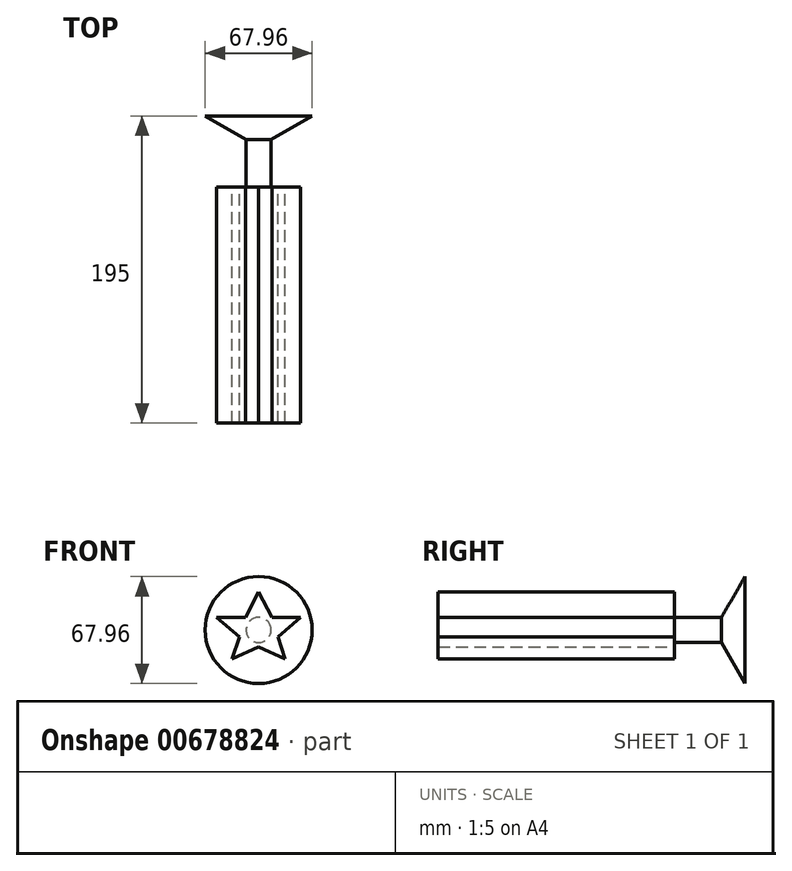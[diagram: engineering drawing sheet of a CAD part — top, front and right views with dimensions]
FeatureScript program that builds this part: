
annotation { "Feature Type Name" : "Feature", "Feature Type Description" : "" }
export const myFeature = defineFeature(function(context is Context, id is Id, definition is map)
    precondition{}
    {
        {
            var Q0;
            Q0=qCreatedBy(makeId("Front.planeOp"),FACE);
            var sketch = newSketch(context, id + "F0", { "sketchPlane" : qUnion([Q0])});
            skLineSegment(sketch, "E0", {"start": v(0, 24.1) * mm, "end": v(8.38, 8) * mm});
            skLineSegment(sketch, "E1", {"start": v(8.38, 8) * mm, "end": v(26.77, 8) * mm});
            skLineSegment(sketch, "E2", {"start": v(26.77, 8) * mm, "end": v(12.19, -4.45) * mm});
            skLineSegment(sketch, "E3", {"start": v(12.19, -4.45) * mm, "end": v(16.83, -18.28) * mm});
            skLineSegment(sketch, "E4", {"start": v(16.83, -18.28) * mm, "end": v(0, -10.61) * mm});
            skLineSegment(sketch, "E5.MirrorCS", {"start": v(0, 24.1) * mm, "end": v(-8.38, 8) * mm});
            skLineSegment(sketch, "E6.MirrorCS", {"start": v(-8.38, 8) * mm, "end": v(-26.77, 8) * mm});
            skLineSegment(sketch, "E7.MirrorCS", {"start": v(-26.77, 8) * mm, "end": v(-12.19, -4.45) * mm});
            skLineSegment(sketch, "E8.MirrorCS", {"start": v(-12.19, -4.45) * mm, "end": v(-16.83, -18.28) * mm});
            skLineSegment(sketch, "E9.MirrorCS", {"start": v(-16.83, -18.28) * mm, "end": v(0, -10.61) * mm});
            skSolve(sketch);
        }
        {
            var Q0;
            Q0=makeQuery(id+"F0.imprint","IMPRINT",FACE,{"disambiguationData":[TD([[makeQuery(id+"F0.imprint","IMPRINT",EDGE,{"derivedFrom":sQuery(id+"F0.wireOp",EDGE,"E0")}),-1.0]])]});
            extrude(context, id + "F1", {"entities" : qUnion([Q0]), "depth" : 150 * mm, "offsetDistance" : 25 * mm});
        }
        {
            var Q0;
            Q0=makeQuery(id+"F1.opExtrude","CAP_FACE",FACE,{"disambiguationData":[OSD([sQuery(id+"F0.wireOp",EDGE,"E0"),sQuery(id+"F0.wireOp",EDGE,"E1"),sQuery(id+"F0.wireOp",EDGE,"E2"),sQuery(id+"F0.wireOp",EDGE,"E3"),sQuery(id+"F0.wireOp",EDGE,"E4"),sQuery(id+"F0.wireOp",EDGE,"E5.MirrorCS"),sQuery(id+"F0.wireOp",EDGE,"E6.MirrorCS"),sQuery(id+"F0.wireOp",EDGE,"E7.MirrorCS"),sQuery(id+"F0.wireOp",EDGE,"E8.MirrorCS"),sQuery(id+"F0.wireOp",EDGE,"E9.MirrorCS")])],"isStart":true});
            var sketch = newSketch(context, id + "F2", { "sketchPlane" : qUnion([Q0])});
            skCircle(sketch, "E10", {"center": v(0, 0) * mm, "radius": 8 * mm});
            skSolve(sketch);
        }
        {
            var Q0;
            Q0=makeQuery(id+"F2.imprint","IMPRINT",FACE,{"disambiguationData":[TD([[makeQuery(id+"F2.imprint","IMPRINT",EDGE,{"derivedFrom":sQuery(id+"F2.wireOp",EDGE,"E10")}),1.0]])]});
            extrude(context, id + "F3", {"entities" : qUnion([Q0]), "operationType" : NewBodyOperationType.ADD, "depth" : 30 * mm, "offsetDistance" : 25 * mm});
        }
        {
            var Q0;
            Q0=makeQuery(id+"F3.opExtrude","CAP_FACE",FACE,{"disambiguationData":[OSD([sQuery(id+"F2.wireOp",EDGE,"E10")])],"isStart":false});
            extrude(context, id + "F4", {"entities" : qUnion([Q0]), "operationType" : NewBodyOperationType.ADD, "depth" : 15 * mm, "offsetDistance" : 25 * mm, "hasDraft" : true, "draftAngle" : 60 * degree});
        }
    });
